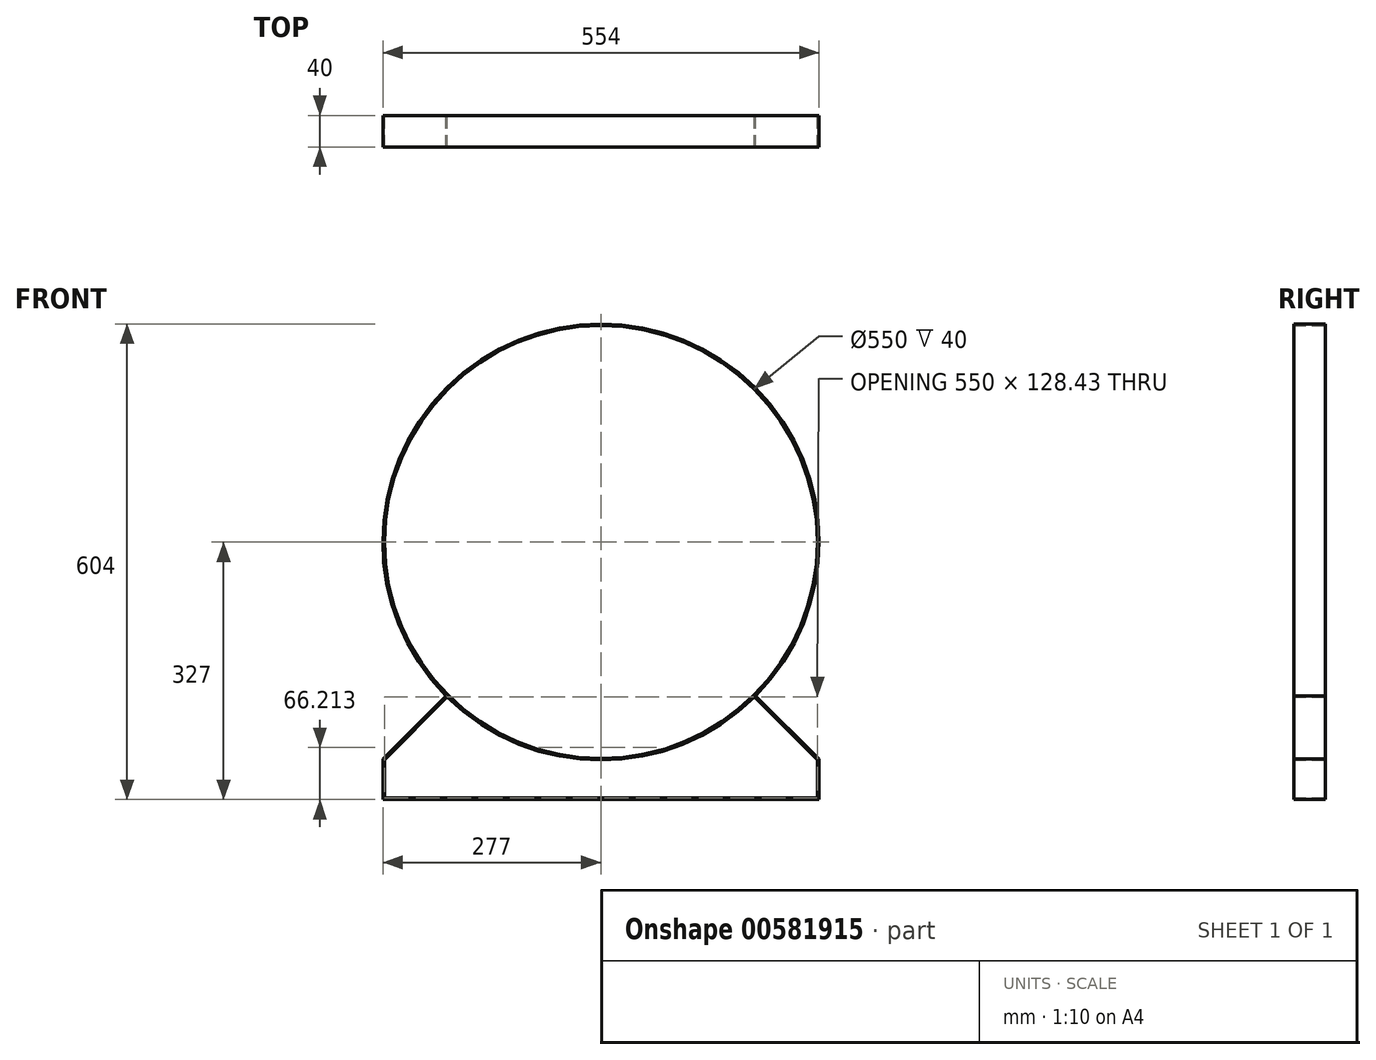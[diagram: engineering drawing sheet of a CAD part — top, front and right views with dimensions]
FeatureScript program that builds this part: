
annotation { "Feature Type Name" : "Feature", "Feature Type Description" : "" }
export const myFeature = defineFeature(function(context is Context, id is Id, definition is map)
    precondition{}
    {
        {
            var Q0;
            Q0=qCreatedBy(makeId("Front.planeOp"),FACE);
            var sketch = newSketch(context, id + "F0", { "sketchPlane" : qUnion([Q0])});
            skLineSegment(sketch, "E0", {"start": v(0, 0) * mm, "end": v(-679.96, 0) * mm, "construction": true});
            skLineSegment(sketch, "E1", {"start": v(0, 0) * mm, "end": v(0, 658.78) * mm, "construction": true});
            skLineSegment(sketch, "E2", {"start": v(0, 0) * mm, "end": v(-291.77, -291.77) * mm, "construction": true});
            skLineSegment(sketch, "E3", {"start": v(0, 0) * mm, "end": v(291.77, -291.77) * mm, "construction": true});
            skCircle(sketch, "E4", {"center": v(0, 0) * mm, "radius": 275 * mm});
            skCircle(sketch, "E5", {"center": v(0, 0) * mm, "radius": 277 * mm});
            skLineSegment(sketch, "E6", {"start": v(-277, -327) * mm, "end": v(0, -327) * mm});
            skLineSegment(sketch, "E7", {"start": v(-275, -325) * mm, "end": v(0, -325) * mm});
            skLineSegment(sketch, "E8", {"start": v(0, 0) * mm, "end": v(0, -311.11) * mm, "construction": true});
            skLineSegment(sketch, "E9", {"start": v(-275, -325) * mm, "end": v(-275, -276.41) * mm});
            skLineSegment(sketch, "E10", {"start": v(-277, -327) * mm, "end": v(-277, -275.59) * mm});
            skLineSegment(sketch, "E11", {"start": v(-196.57, -195.16) * mm, "end": v(-277, -275.59) * mm});
            skLineSegment(sketch, "E12", {"start": v(-195.16, -196.57) * mm, "end": v(-275, -276.41) * mm});
            skLineSegment(sketch, "E13.MirrorCS", {"start": v(195.16, -196.57) * mm, "end": v(275, -276.41) * mm});
            skLineSegment(sketch, "E14.MirrorCS", {"start": v(277, -327) * mm, "end": v(0, -327) * mm});
            skLineSegment(sketch, "E15.MirrorCS", {"start": v(275, -325) * mm, "end": v(0, -325) * mm});
            skLineSegment(sketch, "E16.MirrorCS", {"start": v(196.57, -195.16) * mm, "end": v(277, -275.59) * mm});
            skLineSegment(sketch, "E17.MirrorCS", {"start": v(275, -325) * mm, "end": v(275, -276.41) * mm});
            skLineSegment(sketch, "E18.MirrorCS", {"start": v(277, -327) * mm, "end": v(277, -275.59) * mm});
            skSolve(sketch);
        }
        {
            var Q0;
            Q0=qSketchRegion(id+"F0",true);
            extrude(context, id + "F1", {"entities" : qUnion([Q0]), "offsetDistance" : 25 * mm, "depth" : 40 * mm});
        }
    });
